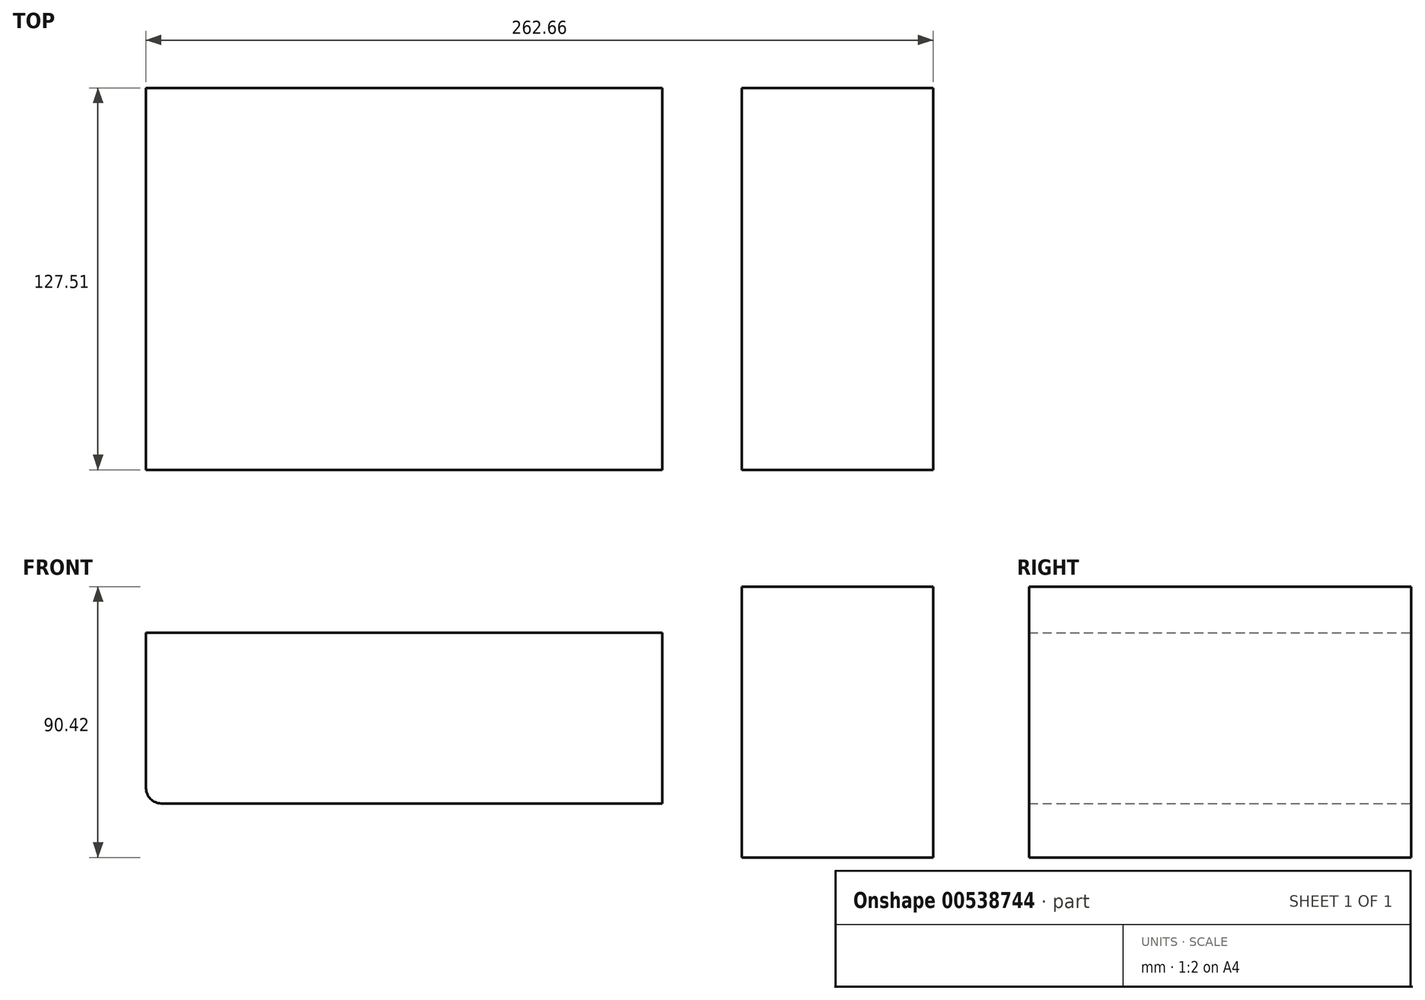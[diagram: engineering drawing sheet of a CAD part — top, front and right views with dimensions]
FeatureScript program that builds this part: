
annotation { "Feature Type Name" : "Feature", "Feature Type Description" : "" }
export const myFeature = defineFeature(function(context is Context, id is Id, definition is map)
    precondition{}
    {
        {
            var Q0;
            Q0=qCreatedBy(makeId("Front.planeOp"),FACE);
            var sketch = newSketch(context, id + "F0", { "sketchPlane" : qUnion([Q0])});
            skLineSegment(sketch, "E0.bottom", {"start": v(-94.27, 39.63) * mm, "end": v(77.98, 39.63) * mm});
            skLineSegment(sketch, "E0.top", {"start": v(-94.27, -17.34) * mm, "end": v(77.98, -17.34) * mm});
            skLineSegment(sketch, "E0.left", {"start": v(-94.27, 39.63) * mm, "end": v(-94.27, -17.34) * mm});
            skLineSegment(sketch, "E0.right", {"start": v(77.98, 39.63) * mm, "end": v(77.98, -17.34) * mm});
            skLineSegment(sketch, "E1.bottom", {"start": v(104.55, -35.38) * mm, "end": v(168.4, -35.38) * mm});
            skLineSegment(sketch, "E1.top", {"start": v(104.55, 55.04) * mm, "end": v(168.4, 55.04) * mm});
            skLineSegment(sketch, "E1.left", {"start": v(104.55, -35.38) * mm, "end": v(104.55, 55.04) * mm});
            skLineSegment(sketch, "E1.right", {"start": v(168.4, -35.38) * mm, "end": v(168.4, 55.04) * mm});
            skSolve(sketch);
        }
        {
            var Q0;
            Q0 = qSketchRegion(id + "F0", true);
            extrude(context, id + "F1", {"entities" : qUnion([Q0]), "depth" : 127.5 * mm, "offsetDistance" : 25.4 * mm});
        }
        {
            var Q0;
            Q0=makeQuery(id+"F1.opExtrude","SWEPT_EDGE",EDGE,{"disambiguationData":[OSD([sQuery(id+"F0.wireOp",EDGE,"E0.top"),sQuery(id+"F0.wireOp",EDGE,"E0.left")])]});
            fillet(context, id + "F2", {"entities" : qUnion([Q0]), "radius" : 5.08 * mm, "tangentPropagation" : true, "allowEdgeOverflow" : false});
        }
    });
